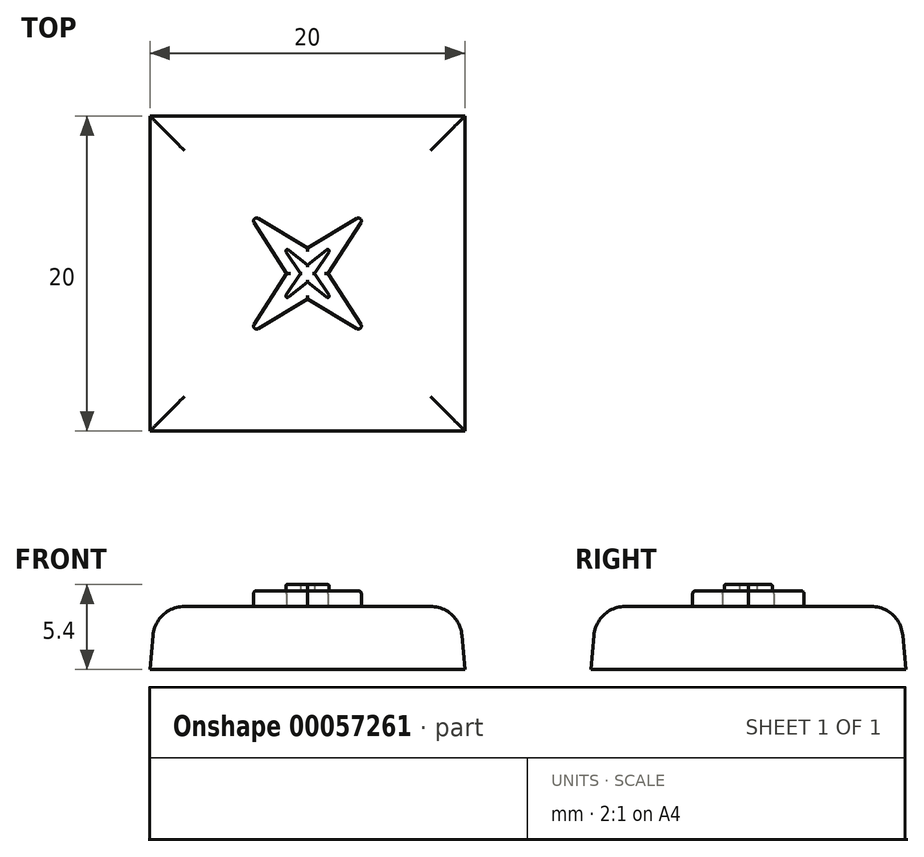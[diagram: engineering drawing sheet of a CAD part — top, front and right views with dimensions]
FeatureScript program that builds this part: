
annotation { "Feature Type Name" : "Feature", "Feature Type Description" : "" }
export const myFeature = defineFeature(function(context is Context, id is Id, definition is map)
    precondition{}
    {
        {
            var Q0;
            Q0=qCreatedBy(makeId("Top.planeOp"),FACE);
            var sketch = newSketch(context, id + "F0", { "sketchPlane" : qUnion([Q0])});
            skLineSegment(sketch, "E0.rect.bottom", {"start": v(10, 10) * mm, "end": v(-10, 10) * mm});
            skLineSegment(sketch, "E0.rect.top", {"start": v(10, -10) * mm, "end": v(-10, -10) * mm});
            skLineSegment(sketch, "E0.rect.left", {"start": v(10, 10) * mm, "end": v(10, -10) * mm});
            skLineSegment(sketch, "E0.rect.right", {"start": v(-10, 10) * mm, "end": v(-10, -10) * mm});
            skPoint(sketch, "E0.rect.middle", {"position": v(0, 0) * mm});
            skSolve(sketch);
        }
        {
            var Q0;
            Q0 = qSketchRegion(id + "F0", true);
            extrude(context, id + "F1", {"entities" : qUnion([Q0]), "depth" : 4 * mm, "hasDraft" : true, "draftAngle" : 5 * degree, "draftPullDirection" : true});
        }
        {
            var Q0;
            Q0=makeQuery(id+"F1.opExtrude","CAP_FACE",FACE,{"disambiguationData":[OSD([sQuery(id+"F0.wireOp",EDGE,"E0.rect.bottom"),sQuery(id+"F0.wireOp",EDGE,"E0.rect.top"),sQuery(id+"F0.wireOp",EDGE,"E0.rect.left"),sQuery(id+"F0.wireOp",EDGE,"E0.rect.right")])],"isStart":false});
            fillet(context, id + "F2", {"entities" : qUnion([Q0]), "radius" : 2 * mm, "tangentPropagation" : true, "allowEdgeOverflow" : false});
        }
        {
            var Q0;
            Q0=makeQuery(id+"F1.opExtrude","CAP_FACE",FACE,{"disambiguationData":[OSD([sQuery(id+"F0.wireOp",EDGE,"E0.rect.bottom"),sQuery(id+"F0.wireOp",EDGE,"E0.rect.top"),sQuery(id+"F0.wireOp",EDGE,"E0.rect.left"),sQuery(id+"F0.wireOp",EDGE,"E0.rect.right")])],"isStart":false});
            var sketch = newSketch(context, id + "F3", { "sketchPlane" : qUnion([Q0])});
            skLineSegment(sketch, "E1", {"start": v(0, 5.87) * mm, "end": v(0, -5.93) * mm, "construction": true});
            skLineSegment(sketch, "E2", {"start": v(-6.5, 0) * mm, "end": v(6.65, 0) * mm, "construction": true});
            skLineSegment(sketch, "E3", {"start": v(0, 1.63) * mm, "end": v(-3.85, 3.95) * mm});
            skLineSegment(sketch, "E4", {"start": v(-3.85, 3.95) * mm, "end": v(-1.32, 0) * mm});
            skLineSegment(sketch, "E5.MirrorCS", {"start": v(0, 1.63) * mm, "end": v(3.85, 3.95) * mm});
            skLineSegment(sketch, "E6.MirrorCS", {"start": v(3.85, 3.95) * mm, "end": v(1.32, 0) * mm});
            skLineSegment(sketch, "E7.MirrorCS", {"start": v(-3.85, -3.95) * mm, "end": v(-1.32, 0) * mm});
            skLineSegment(sketch, "E8.MirrorCS", {"start": v(0, -1.63) * mm, "end": v(-3.85, -3.95) * mm});
            skLineSegment(sketch, "E9.MirrorCS", {"start": v(0, -1.63) * mm, "end": v(3.85, -3.95) * mm});
            skLineSegment(sketch, "E10.MirrorCS", {"start": v(3.85, -3.95) * mm, "end": v(1.32, 0) * mm});
            skSolve(sketch);
        }
        {
            var Q0;
            Q0=makeQuery(id+"F3.imprint","IMPRINT",FACE,{"disambiguationData":[TD([[makeQuery(id+"F3.imprint","IMPRINT",EDGE,{"derivedFrom":sQuery(id+"F3.wireOp",EDGE,"E3")}),1.0]])]});
            extrude(context, id + "F4", {"entities" : qUnion([Q0]), "operationType" : NewBodyOperationType.ADD, "depth" : 1 * mm});
        }
        {
            var Q0;
            Q0=makeQuery(id+"F4.opExtrude","CAP_FACE",FACE,{"disambiguationData":[OSD([sQuery(id+"F3.wireOp",EDGE,"E3"),sQuery(id+"F3.wireOp",EDGE,"E4"),sQuery(id+"F3.wireOp",EDGE,"E5.MirrorCS"),sQuery(id+"F3.wireOp",EDGE,"E6.MirrorCS"),sQuery(id+"F3.wireOp",EDGE,"E7.MirrorCS"),sQuery(id+"F3.wireOp",EDGE,"E8.MirrorCS"),sQuery(id+"F3.wireOp",EDGE,"E9.MirrorCS"),sQuery(id+"F3.wireOp",EDGE,"E10.MirrorCS")])],"isStart":false});
            var Q1;
            Q1=makeQuery(id+"F4.opExtrude","SWEPT_EDGE",EDGE,{"disambiguationData":[OSD([sQuery(id+"F3.wireOp",EDGE,"E3"),sQuery(id+"F3.wireOp",EDGE,"E4")])]});
            var Q2;
            Q2=makeQuery(id+"F4.opExtrude","SWEPT_EDGE",EDGE,{"disambiguationData":[OSD([sQuery(id+"F3.wireOp",EDGE,"E7.MirrorCS"),sQuery(id+"F3.wireOp",EDGE,"E8.MirrorCS")])]});
            var Q3;
            Q3=makeQuery(id+"F4.opExtrude","SWEPT_EDGE",EDGE,{"disambiguationData":[OSD([sQuery(id+"F3.wireOp",EDGE,"E5.MirrorCS"),sQuery(id+"F3.wireOp",EDGE,"E6.MirrorCS")])]});
            var Q4;
            Q4=makeQuery(id+"F4.opExtrude","SWEPT_EDGE",EDGE,{"disambiguationData":[OSD([sQuery(id+"F3.wireOp",EDGE,"E9.MirrorCS"),sQuery(id+"F3.wireOp",EDGE,"E10.MirrorCS")])]});
            fillet(context, id + "F5", {"entities" : qUnion([Q0, Q1, Q2, Q3, Q4]), "radius" : 0.2 * mm, "tangentPropagation" : true, "allowEdgeOverflow" : false});
        }
        {
            var Q0;
            Q0=makeQuery(id+"F4.opExtrude","CAP_FACE",FACE,{"disambiguationData":[OSD([sQuery(id+"F3.wireOp",EDGE,"E3"),sQuery(id+"F3.wireOp",EDGE,"E4"),sQuery(id+"F3.wireOp",EDGE,"E5.MirrorCS"),sQuery(id+"F3.wireOp",EDGE,"E6.MirrorCS"),sQuery(id+"F3.wireOp",EDGE,"E7.MirrorCS"),sQuery(id+"F3.wireOp",EDGE,"E8.MirrorCS"),sQuery(id+"F3.wireOp",EDGE,"E9.MirrorCS"),sQuery(id+"F3.wireOp",EDGE,"E10.MirrorCS")])],"isStart":false});
            var sketch = newSketch(context, id + "F6", { "sketchPlane" : qUnion([Q0])});
            skLineSegment(sketch, "E11", {"start": v(0, 3.4) * mm, "end": v(0, -3.8) * mm, "construction": true});
            skLineSegment(sketch, "E12", {"start": v(-4.03, 0) * mm, "end": v(4.1, 0) * mm, "construction": true});
            skLineSegment(sketch, "E13", {"start": v(0, 0.55) * mm, "end": v(-1.7, 1.89) * mm});
            skLineSegment(sketch, "E14", {"start": v(-1.7, 1.89) * mm, "end": v(-0.46, 0) * mm});
            skLineSegment(sketch, "E15.MirrorCS", {"start": v(0, 0.55) * mm, "end": v(1.7, 1.89) * mm});
            skLineSegment(sketch, "E16.MirrorCS", {"start": v(1.7, 1.89) * mm, "end": v(0.46, 0) * mm});
            skLineSegment(sketch, "E17.MirrorCS", {"start": v(1.7, -1.89) * mm, "end": v(0.46, 0) * mm});
            skLineSegment(sketch, "E18.MirrorCS", {"start": v(0, -0.55) * mm, "end": v(1.7, -1.89) * mm});
            skLineSegment(sketch, "E19.MirrorCS", {"start": v(0, -3.4) * mm, "end": v(0, 3.8) * mm, "construction": true});
            skLineSegment(sketch, "E20.MirrorCS", {"start": v(-1.7, -1.89) * mm, "end": v(-0.46, 0) * mm});
            skLineSegment(sketch, "E21.MirrorCS", {"start": v(0, -0.55) * mm, "end": v(-1.7, -1.89) * mm});
            skSolve(sketch);
        }
        {
            var Q0;
            Q0=makeQuery(id+"F6.imprint","IMPRINT",FACE,{"disambiguationData":[TD([[makeQuery(id+"F6.imprint","IMPRINT",EDGE,{"derivedFrom":sQuery(id+"F6.wireOp",EDGE,"E13")}),1.0]])]});
            extrude(context, id + "F7", {"entities" : qUnion([Q0]), "operationType" : NewBodyOperationType.ADD, "depth" : 0.4 * mm});
        }
        {
            var Q0;
            Q0=makeQuery(id+"F7.opExtrude","CAP_FACE",FACE,{"disambiguationData":[OSD([sQuery(id+"F6.wireOp",EDGE,"E13"),sQuery(id+"F6.wireOp",EDGE,"E14"),sQuery(id+"F6.wireOp",EDGE,"E15.MirrorCS"),sQuery(id+"F6.wireOp",EDGE,"E16.MirrorCS"),sQuery(id+"F6.wireOp",EDGE,"E17.MirrorCS"),sQuery(id+"F6.wireOp",EDGE,"E18.MirrorCS"),sQuery(id+"F6.wireOp",EDGE,"E20.MirrorCS"),sQuery(id+"F6.wireOp",EDGE,"E21.MirrorCS")])],"isStart":false});
            var Q1;
            Q1=makeQuery(id+"F7.opExtrude","SWEPT_EDGE",EDGE,{"disambiguationData":[OSD([sQuery(id+"F6.wireOp",EDGE,"E15.MirrorCS"),sQuery(id+"F6.wireOp",EDGE,"E16.MirrorCS")])]});
            var Q2;
            Q2=makeQuery(id+"F7.opExtrude","SWEPT_EDGE",EDGE,{"disambiguationData":[OSD([sQuery(id+"F6.wireOp",EDGE,"E17.MirrorCS"),sQuery(id+"F6.wireOp",EDGE,"E18.MirrorCS")])]});
            var Q3;
            Q3=makeQuery(id+"F7.opExtrude","SWEPT_EDGE",EDGE,{"disambiguationData":[OSD([sQuery(id+"F6.wireOp",EDGE,"E20.MirrorCS"),sQuery(id+"F6.wireOp",EDGE,"E21.MirrorCS")])]});
            var Q4;
            Q4=makeQuery(id+"F7.opExtrude","SWEPT_EDGE",EDGE,{"disambiguationData":[OSD([sQuery(id+"F6.wireOp",EDGE,"E13"),sQuery(id+"F6.wireOp",EDGE,"E14")])]});
            fillet(context, id + "F8", {"entities" : qUnion([Q0, Q1, Q2, Q3, Q4]), "radius" : 0.1 * mm, "tangentPropagation" : true, "allowEdgeOverflow" : false});
        }
    });
